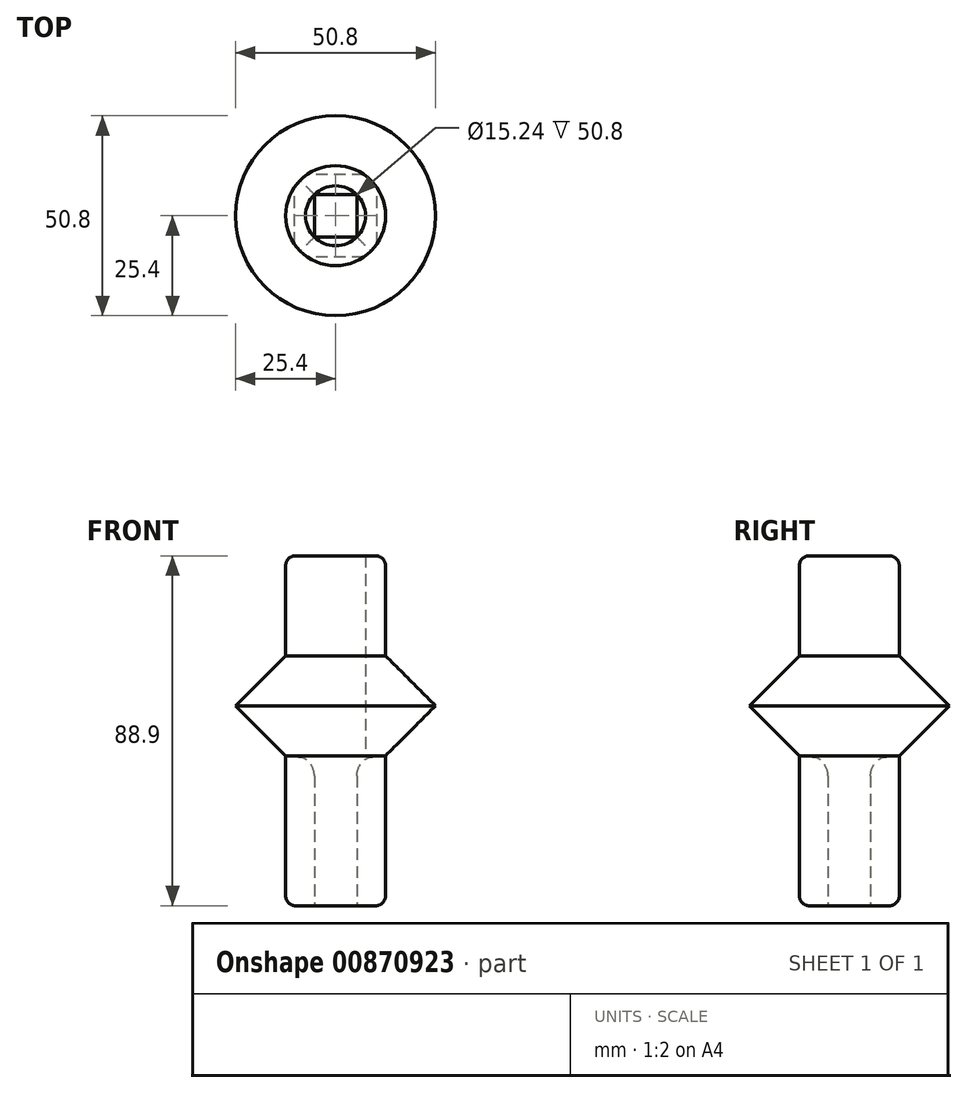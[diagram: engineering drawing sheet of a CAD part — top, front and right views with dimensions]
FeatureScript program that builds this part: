
annotation { "Feature Type Name" : "Feature", "Feature Type Description" : "" }
export const myFeature = defineFeature(function(context is Context, id is Id, definition is map)
    precondition{}
    {
        {
            var Q0;
            Q0=qCreatedBy(makeId("Top.planeOp"),FACE);
            var sketch = newSketch(context, id + "F0", { "sketchPlane" : qUnion([Q0])});
            skCircle(sketch, "E0", {"center": v(0, 0) * mm, "radius": 12.7 * mm});
            skCircle(sketch, "E1", {"center": v(0, 0) * mm, "radius": 7.62 * mm});
            skLineSegment(sketch, "E2.bottom", {"start": v(5.39, -5.39) * mm, "end": v(-5.39, -5.39) * mm});
            skLineSegment(sketch, "E2.top", {"start": v(5.39, 5.39) * mm, "end": v(-5.39, 5.39) * mm});
            skLineSegment(sketch, "E2.left", {"start": v(5.39, -5.39) * mm, "end": v(5.39, 5.39) * mm});
            skLineSegment(sketch, "E2.right", {"start": v(-5.39, -5.39) * mm, "end": v(-5.39, 5.39) * mm});
            skSolve(sketch);
        }
        {
            var Q0;
            Q0=makeQuery(id+"F0.imprint","IMPRINT",FACE,{"disambiguationData":[TD([[makeQuery(id+"F0.imprint","IMPRINT",EDGE,{"derivedFrom":sQuery(id+"F0.wireOp",EDGE,"E0")}),1.0]])]});
            var Q1;
            {var subQ0=sQuery(id+"F0.wireOp",EDGE,"E2.bottom");Q1=makeQuery(id+"F0.imprint","IMPRINT",FACE,{"disambiguationData":[TD([[makeQuery(id+"F0.imprint","IMPRINT",EDGE,{"derivedFrom":subQ0}),1.0]])]});}
            var Q2;
            {var subQ0=sQuery(id+"F0.wireOp",EDGE,"E2.right");Q2=makeQuery(id+"F0.imprint","IMPRINT",FACE,{"disambiguationData":[TD([[makeQuery(id+"F0.imprint","IMPRINT",EDGE,{"derivedFrom":subQ0}),1.0]])]});}
            var Q3;
            {var subQ0=sQuery(id+"F0.wireOp",EDGE,"E2.left");Q3=makeQuery(id+"F0.imprint","IMPRINT",FACE,{"disambiguationData":[TD([[makeQuery(id+"F0.imprint","IMPRINT",EDGE,{"derivedFrom":subQ0}),-1.0]])]});}
            var Q4;
            {var subQ0=sQuery(id+"F0.wireOp",EDGE,"E2.top");Q4=makeQuery(id+"F0.imprint","IMPRINT",FACE,{"disambiguationData":[TD([[makeQuery(id+"F0.imprint","IMPRINT",EDGE,{"derivedFrom":subQ0}),-1.0]])]});}
            extrude(context, id + "F1", {"entities" : qUnion([Q0, Q1, Q2, Q3, Q4]), "flatOperationType" : FlatOperationType.REMOVE, "depth" : 38.1 * mm, "offsetDistance" : 25.4 * mm, "domain" : OperationDomain.MODEL});
        }
        {
            var Q0;
            Q0=makeQuery(id+"F1.opExtrude","CAP_FACE",FACE,{"disambiguationData":[OSD([sQuery(id+"F0.wireOp",EDGE,"E0"),sQuery(id+"F0.wireOp",EDGE,"E1")])],"isStart":false});
            var sketch = newSketch(context, id + "F2", { "sketchPlane" : qUnion([Q0])});
            skCircle(sketch, "E3", {"center": v(0, 0) * mm, "radius": 25.4 * mm});
            skSolve(sketch);
        }
        {
            var Q0;
            Q0=makeQuery(id+"F2.imprint","IMPRINT",FACE,{"disambiguationData":[TD([[makeQuery(id+"F2.imprint","IMPRINT",EDGE,{"derivedFrom":sQuery(id+"F2.wireOp",EDGE,"E3")}),1.0]])]});
            extrude(context, id + "F3", {"entities" : qUnion([Q0]), "depth" : 12.7 * mm, "offsetDistance" : 25.4 * mm});
        }
        {
            var Q0;
            Q0=makeQuery(id+"F1.opExtrude","CAP_EDGE",EDGE,{"disambiguationData":[OSD([sQuery(id+"F0.wireOp",EDGE,"E0")])],"isStart":true});
            fillet(context, id + "F4", {"entities" : qUnion([Q0]), "radius" : 2.54 * mm, "tangentPropagation" : true, "allowEdgeOverflow" : false});
        }
        {
            var Q0;
            Q0=makeQuery(id+"F1.opExtrude","CAP_EDGE",EDGE,{"disambiguationData":[OSD([sQuery(id+"F0.wireOp",EDGE,"E2.left")])],"isStart":false});
            var Q1;
            Q1=makeQuery(id+"F1.opExtrude","CAP_EDGE",EDGE,{"disambiguationData":[OSD([sQuery(id+"F0.wireOp",EDGE,"E2.bottom")])],"isStart":false});
            var Q2;
            Q2=makeQuery(id+"F1.opExtrude","CAP_EDGE",EDGE,{"disambiguationData":[OSD([sQuery(id+"F0.wireOp",EDGE,"E2.right")])],"isStart":false});
            var Q3;
            Q3=makeQuery(id+"F1.opExtrude","CAP_EDGE",EDGE,{"disambiguationData":[OSD([sQuery(id+"F0.wireOp",EDGE,"E2.top")])],"isStart":false});
            fillet(context, id + "F5", {"entities" : qUnion([Q0, Q1, Q2, Q3]), "radius" : 5.08 * mm, "tangentPropagation" : true, "allowEdgeOverflow" : false});
        }
        {
            var Q0;
            Q0=makeQuery(id+"F3.opExtrude","SWEPT_BODY",BODY,{"disambiguationData":[OSD([sQuery(id+"F0.wireOp",EDGE,"E0"),sQuery(id+"F2.wireOp",EDGE,"E3")])]});
            var Q1;
            Q1=makeQuery(id+"F3.opExtrude","CAP_FACE",FACE,{"disambiguationData":[OSD([sQuery(id+"F0.wireOp",EDGE,"E0"),sQuery(id+"F2.wireOp",EDGE,"E3")])],"isStart":false});
            mirror(context, id + "F6", {"operationType" : NewBodyOperationType.ADD, "entities" : qUnion([Q0]), "mirrorPlane" : qUnion([Q1])});
        }
        {
            var Q0;
            Q0=makeQuery(id+"F5.opFillet","SPLIT",FACE,{"disambiguationData":[OD(1.0)],"derivedFrom":makeQuery(id+"F1.opExtrude","CAP_FACE",FACE,{"disambiguationData":[OSD([sQuery(id+"F0.wireOp",EDGE,"E0"),sQuery(id+"F0.wireOp",EDGE,"E2.bottom"),sQuery(id+"F0.wireOp",EDGE,"E2.top"),sQuery(id+"F0.wireOp",EDGE,"E2.left"),sQuery(id+"F0.wireOp",EDGE,"E2.right")])],"isStart":false})});
            cPlane(context, id + "F7", {"entities" : qUnion([Q0]), "cplaneType" : CPlaneType.OFFSET, "offset" : 25.4 * mm, "width" : 152.4 * mm, "height" : 152.4 * mm});
        }
        {
            var Q0;
            Q0=qCreatedBy(id+"F7.planeOp",FACE);
            var sketch = newSketch(context, id + "F8", { "sketchPlane" : qUnion([Q0])});
            skCircle(sketch, "E4", {"center": v(0, 0) * mm, "radius": 12.7 * mm});
            skCircle(sketch, "E5", {"center": v(0, 0) * mm, "radius": 7.62 * mm});
            skSolve(sketch);
        }
        {
            var Q0;
            Q0=makeQuery(id+"F8.imprint","IMPRINT",FACE,{"disambiguationData":[TD([[makeQuery(id+"F8.imprint","IMPRINT",EDGE,{"derivedFrom":sQuery(id+"F8.wireOp",EDGE,"E4")}),1.0]])]});
            extrude(context, id + "F9", {"entities" : qUnion([Q0]), "depth" : 25.4 * mm, "offsetDistance" : 25.4 * mm});
        }
        {
            var Q0;
            Q0=makeQuery(id+"F9.opExtrude","CAP_EDGE",EDGE,{"disambiguationData":[OSD([sQuery(id+"F8.wireOp",EDGE,"E4")])],"isStart":false});
            fillet(context, id + "F10", {"entities" : qUnion([Q0]), "radius" : 2.54 * mm, "tangentPropagation" : true, "allowEdgeOverflow" : false});
        }
        {
            var Q0;
            Q0=qSketchRegion(id+"F8",true);
            extrude(context, id + "F11", {"entities" : qUnion([Q0]), "operationType" : NewBodyOperationType.ADD, "oppositeDirection" : true, "depth" : 25.4 * mm, "offsetDistance" : 25.4 * mm});
        }
        {
            var Q0;
            Q0=makeQuery(id+"F3.opExtrude","CAP_EDGE",EDGE,{"disambiguationData":[OSD([sQuery(id+"F2.wireOp",EDGE,"E3")])],"isStart":true});
            var Q1;
            Q1=makeQuery(id+"F6.opPattern","COPY",EDGE,{"derivedFrom":makeQuery(id+"F3.opExtrude","CAP_EDGE",EDGE,{"disambiguationData":[OSD([sQuery(id+"F2.wireOp",EDGE,"E3")])],"isStart":true}),"instanceName":"1"});
            chamfer(context, id + "F12", {"entities" : qUnion([Q0, Q1]), "width" : 12.7 * mm, "tangentPropagation" : true});
        }
    });
